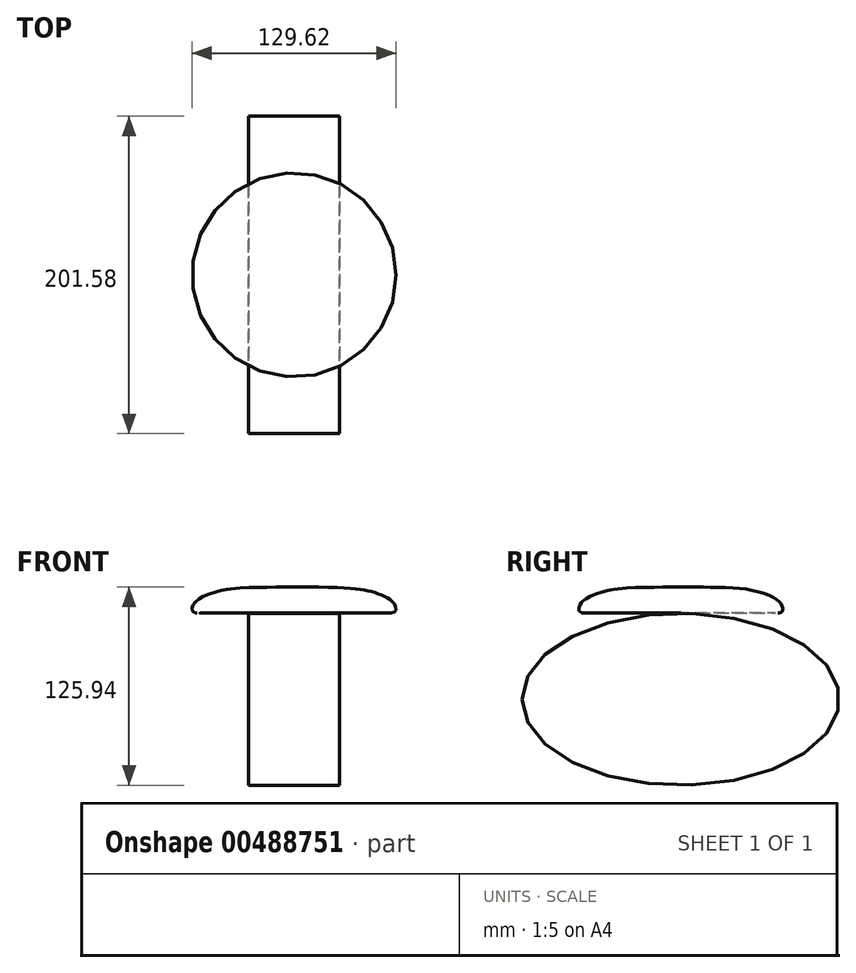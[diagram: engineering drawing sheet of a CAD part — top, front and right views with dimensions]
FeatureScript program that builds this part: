
annotation { "Feature Type Name" : "Feature", "Feature Type Description" : "" }
export const myFeature = defineFeature(function(context is Context, id is Id, definition is map)
    precondition{}
    {
        {
            var Q0;
            Q0=qCreatedBy(makeId("Front.planeOp"),FACE);
            var sketch = newSketch(context, id + "F0", { "sketchPlane" : qUnion([Q0])});
            skLineSegment(sketch, "E0", {"start": v(0, 16.45) * mm, "end": v(0, 0) * mm});
            skLineSegment(sketch, "E1", {"start": v(0, 0) * mm, "end": v(61.64, 0) * mm});
            skFitSpline(sketch, "E2", {"points": [v(0, 16.45) * mm, v(47.47, 13.96) * mm, v(57.75, 10.36) * mm, v(64.26, 4.69) * mm, v(61.64, 0) * mm], "startDerivative": vector(207.2, 0) * mm, "endDerivative": vector(-73.14, 0) * mm});
            skLineSegment(sketch, "E3", {"start": v(0, 16.45) * mm, "end": v(-7.07, 16.45) * mm, "construction": true});
            skSolve(sketch);
        }
        {
            var Q0;
            Q0 = qSketchRegion(id + "F0", true);
            var Q1;
            Q1=sQuery(id+"F0.wireOp",EDGE,"E0");
            revolve(context, id + "F1", {"entities" : qUnion([Q0]), "axis" : qUnion([Q1]), "revolveType" : RevolveType.FULL});
        }
        {
            var Q0;
            Q0=qCreatedBy(makeId("Right.planeOp"),FACE);
            var sketch = newSketch(context, id + "F2", { "sketchPlane" : qUnion([Q0])});
            skEllipse(sketch, "E4", {"center": v(0, -54.88) * mm, "majorRadius": 54.61 * mm, "minorRadius": 100.79 * mm, "majorAxis": v(0, 1)});
            skFitSpline(sketch, "E5.0", {"points": [v(-96.15, -52.58) * mm, v(-96.25, -54.88) * mm, v(-96.15, -57.17) * mm, v(-95.73, -60.2) * mm, v(-94.69, -64) * mm, v(-92.59, -68.53) * mm, v(-89.63, -73.01) * mm, v(-85.8, -77.4) * mm, v(-81.9, -80.95) * mm, v(-78.35, -83.69) * mm, v(-75.48, -85.68) * mm, v(-72.4, -87.62) * mm, v(-69.12, -89.49) * mm, v(-65.66, -91.27) * mm, v(-62.05, -92.96) * mm, v(-58.29, -94.54) * mm, v(-53.09, -96.52) * mm, v(-46.27, -98.73) * mm, v(-37.63, -100.94) * mm, v(-28.62, -102.7) * mm, v(-20.86, -103.75) * mm, v(-14.52, -104.35) * mm, v(-9.72, -104.67) * mm, v(-5.69, -104.84) * mm, v(-2.44, -104.9) * mm, v(0, -104.92) * mm, v(2.44, -104.9) * mm, v(5.69, -104.84) * mm, v(9.72, -104.67) * mm, v(14.52, -104.35) * mm, v(20.86, -103.75) * mm, v(28.62, -102.7) * mm, v(37.63, -100.94) * mm, v(46.27, -98.73) * mm, v(53.09, -96.52) * mm, v(58.29, -94.54) * mm, v(62.05, -92.96) * mm, v(65.66, -91.27) * mm, v(69.12, -89.49) * mm, v(72.4, -87.62) * mm, v(75.48, -85.68) * mm, v(78.35, -83.69) * mm, v(81.9, -80.95) * mm, v(85.8, -77.4) * mm, v(89.63, -73.01) * mm, v(92.59, -68.53) * mm, v(94.69, -64) * mm, v(95.73, -60.2) * mm, v(96.15, -57.17) * mm, v(96.25, -54.88) * mm, v(96.15, -52.58) * mm, v(95.73, -49.54) * mm, v(94.69, -45.75) * mm, v(92.59, -41.22) * mm, v(89.63, -36.74) * mm, v(85.8, -32.34) * mm, v(81.9, -28.8) * mm, v(78.35, -26.06) * mm, v(75.48, -24.07) * mm, v(72.4, -22.13) * mm, v(69.12, -20.27) * mm, v(65.66, -18.48) * mm, v(62.05, -16.8) * mm, v(58.29, -15.2) * mm, v(53.09, -13.23) * mm, v(46.27, -11.02) * mm, v(37.63, -8.8) * mm, v(28.62, -7.06) * mm, v(20.86, -6) * mm, v(14.52, -5.4) * mm, v(9.72, -5.08) * mm, v(5.69, -4.91) * mm, v(2.44, -4.85) * mm, v(0, -4.83) * mm, v(-2.44, -4.85) * mm, v(-5.69, -4.91) * mm, v(-9.72, -5.08) * mm, v(-14.52, -5.4) * mm, v(-20.86, -6) * mm, v(-28.62, -7.06) * mm, v(-37.63, -8.8) * mm, v(-46.27, -11.02) * mm, v(-53.09, -13.23) * mm, v(-58.29, -15.2) * mm, v(-62.05, -16.8) * mm, v(-65.66, -18.48) * mm, v(-69.12, -20.27) * mm, v(-72.4, -22.13) * mm, v(-75.48, -24.07) * mm, v(-78.35, -26.06) * mm, v(-81.9, -28.8) * mm, v(-85.8, -32.34) * mm, v(-89.63, -36.74) * mm, v(-92.59, -41.22) * mm, v(-94.69, -45.75) * mm, v(-95.73, -49.54) * mm, v(-96.15, -52.58) * mm, v(-96.25, -54.88) * mm, v(-96.15, -57.17) * mm, v(-96.15, -52.58) * mm]});
            skSolve(sketch);
        }
        {
            var Q0;
            Q0=makeQuery(id+"F2.imprint","IMPRINT",FACE,{"disambiguationData":[TD([[makeQuery(id+"F2.imprint","IMPRINT",EDGE,{"derivedFrom":sQuery(id+"F2.wireOp",EDGE,"E4")}),1.0]])]});
            extrude(context, id + "F3", {"entities" : qUnion([Q0]), "endBound" : BoundingType.SYMMETRIC, "depth" : 57.9 * mm});
        }
    });
